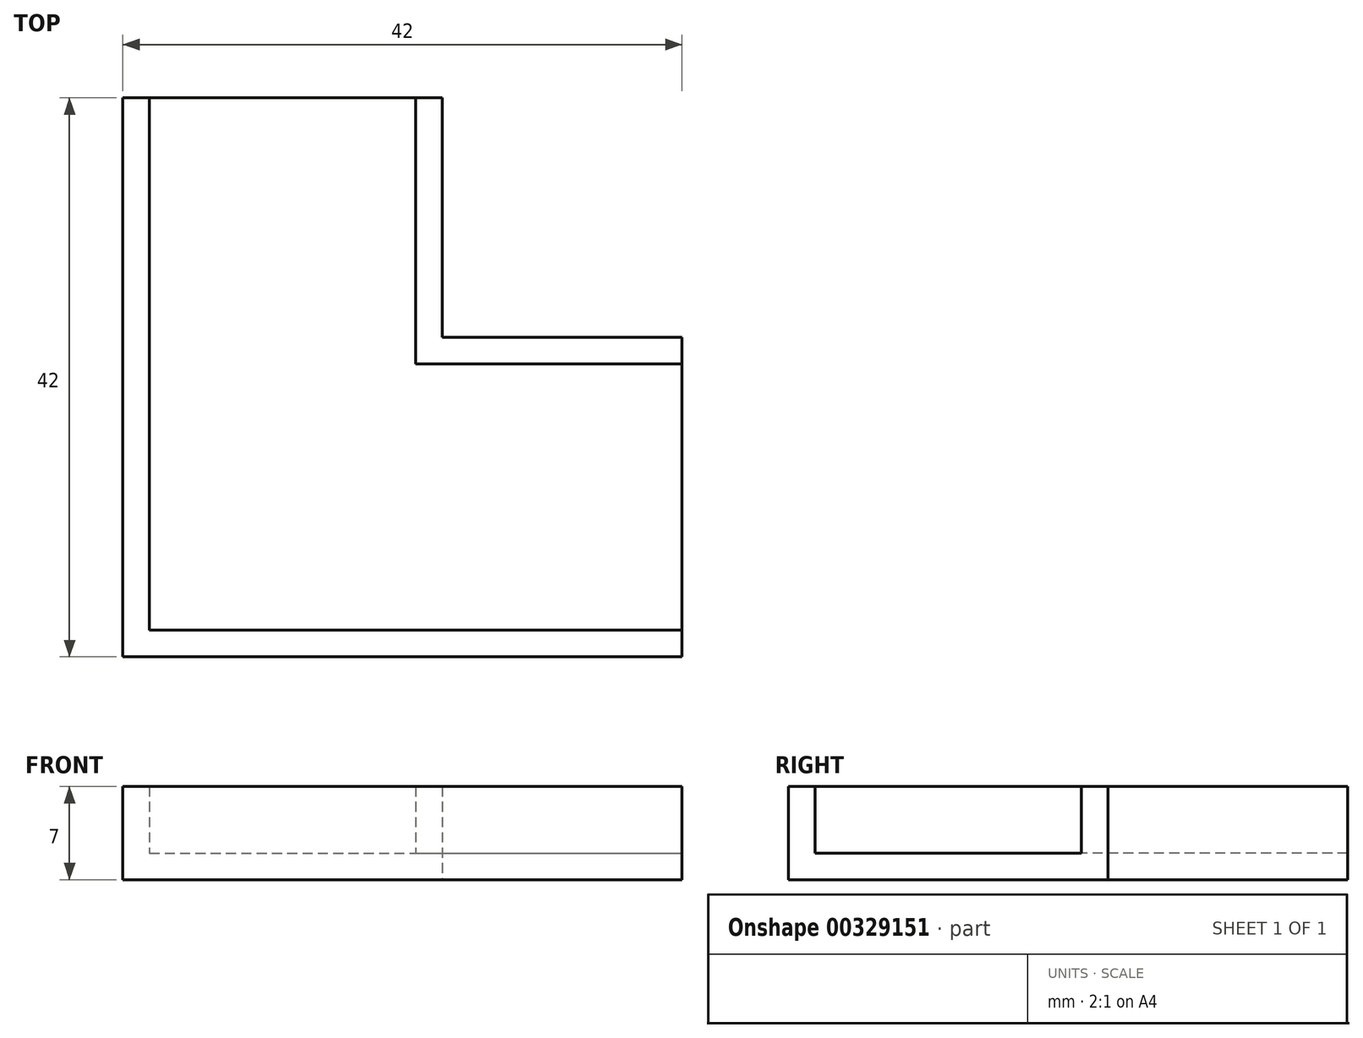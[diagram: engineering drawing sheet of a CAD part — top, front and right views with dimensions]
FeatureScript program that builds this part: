
annotation { "Feature Type Name" : "Feature", "Feature Type Description" : "" }
export const myFeature = defineFeature(function(context is Context, id is Id, definition is map)
    precondition{}
    {
        {
            var Q0;
            Q0=qCreatedBy(makeId("Top.planeOp"),FACE);
            var sketch = newSketch(context, id + "F0", { "sketchPlane" : qUnion([Q0])});
            skLineSegment(sketch, "E0.bottom", {"start": v(-20, 20) * mm, "end": v(0, 20) * mm});
            skLineSegment(sketch, "E0.top", {"start": v(-20, -20) * mm, "end": v(20, -20) * mm});
            skLineSegment(sketch, "E0.left", {"start": v(-20, 20) * mm, "end": v(-20, -20) * mm});
            skLineSegment(sketch, "E0.right", {"start": v(20, 0) * mm, "end": v(20, -20) * mm});
            skPoint(sketch, "E0.middle", {"position": v(0, 0) * mm});
            skLineSegment(sketch, "E1", {"start": v(0, 20) * mm, "end": v(0, 0) * mm});
            skLineSegment(sketch, "E2", {"start": v(0, 0) * mm, "end": v(20, 0) * mm});
            skPoint(sketch, "E3.orphan", {"position": v(20, 20) * mm});
            skSolve(sketch);
        }
        {
            var Q0;
            Q0 = qSketchRegion(id + "F0", true);
            extrude(context, id + "F1", {"entities" : qUnion([Q0]), "depth" : 5 * mm});
        }
        {
            var Q0;
            Q0=makeQuery(id+"F1.opExtrude","CAP_FACE",FACE,{"disambiguationData":[OSD([sQuery(id+"F0.wireOp",EDGE,"E0.bottom"),sQuery(id+"F0.wireOp",EDGE,"E0.top"),sQuery(id+"F0.wireOp",EDGE,"E0.left"),sQuery(id+"F0.wireOp",EDGE,"E0.right"),sQuery(id+"F0.wireOp",EDGE,"E1"),sQuery(id+"F0.wireOp",EDGE,"E2")])],"isStart":false});
            var Q1;
            Q1=makeQuery(id+"F1.opExtrude","SWEPT_FACE",FACE,{"disambiguationData":[OSD([sQuery(id+"F0.wireOp",EDGE,"E0.right")])]});
            var Q2;
            Q2=makeQuery(id+"F1.opExtrude","SWEPT_FACE",FACE,{"disambiguationData":[OSD([sQuery(id+"F0.wireOp",EDGE,"E0.bottom")])]});
            shell(context, id + "F2", {"entities" : qUnion([Q0, Q1, Q2]), "thickness" : 2 * mm, "oppositeDirection" : true});
        }
    });
